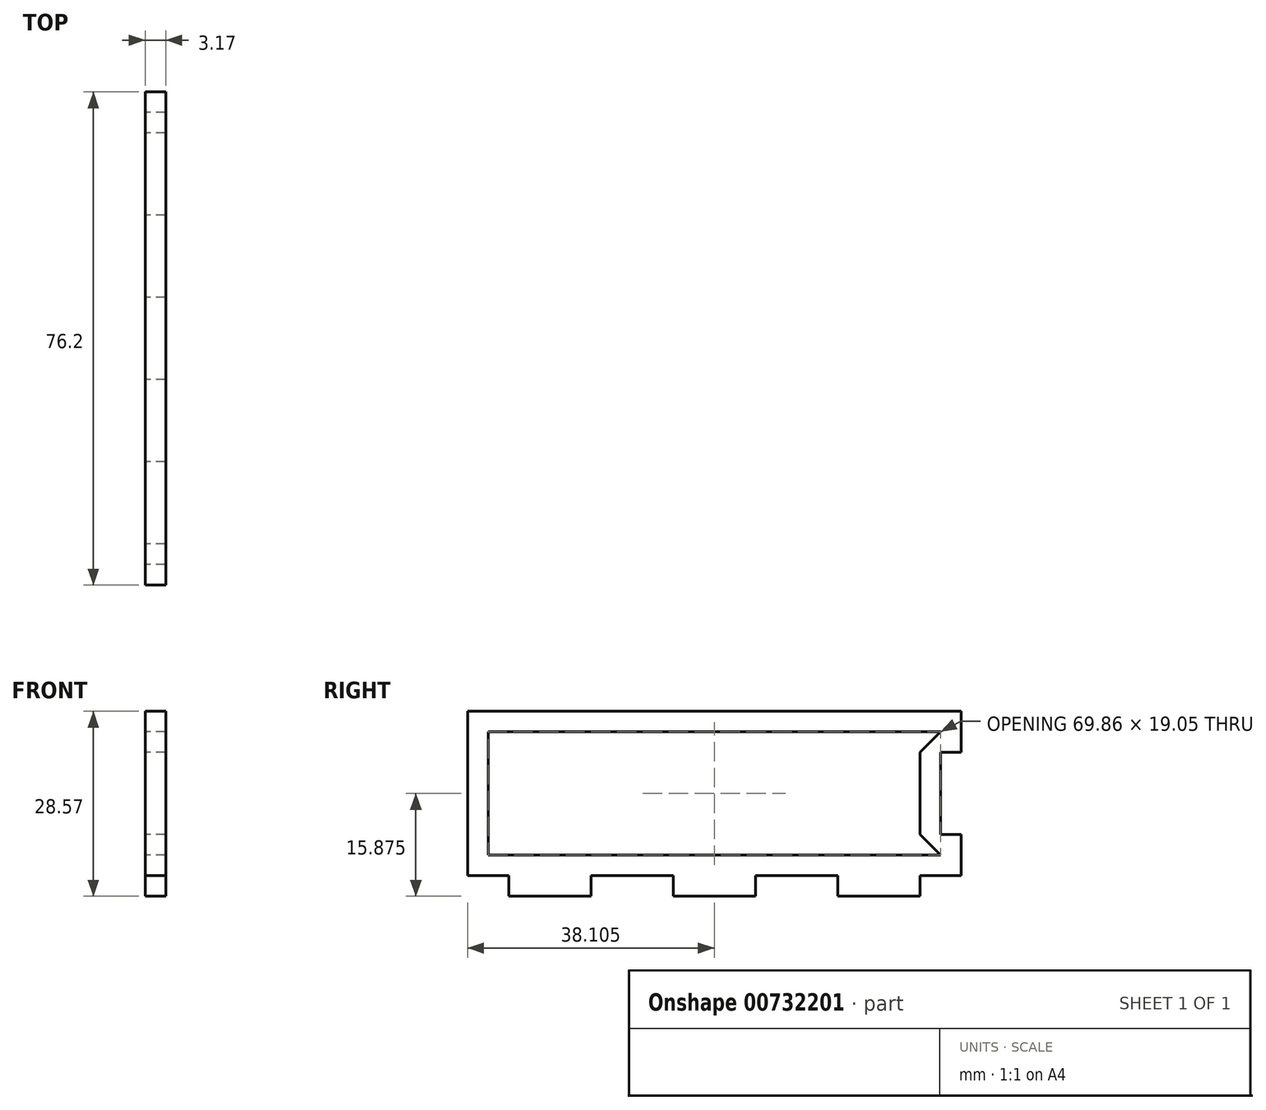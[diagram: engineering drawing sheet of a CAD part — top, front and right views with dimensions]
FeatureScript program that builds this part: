
annotation { "Feature Type Name" : "Feature", "Feature Type Description" : "" }
export const myFeature = defineFeature(function(context is Context, id is Id, definition is map)
    precondition{}
    {
        {
            var Q0;
            Q0=qCreatedBy(makeId("Right.planeOp"),FACE);
            var sketch = newSketch(context, id + "F0", { "sketchPlane" : qUnion([Q0])});
            skLineSegment(sketch, "E0", {"start": v(0, 0) * mm, "end": v(-63.5, 0) * mm});
            skLineSegment(sketch, "E1", {"start": v(-63.5, 0) * mm, "end": v(-63.5, 3.17) * mm});
            skLineSegment(sketch, "E2", {"start": v(-63.5, 3.17) * mm, "end": v(-69.85, 3.17) * mm});
            skLineSegment(sketch, "E3", {"start": v(0, 0) * mm, "end": v(0, 3.18) * mm});
            skLineSegment(sketch, "E4", {"start": v(0, 3.18) * mm, "end": v(6.35, 3.18) * mm});
            skLineSegment(sketch, "E5", {"start": v(6.35, 3.18) * mm, "end": v(6.35, 28.58) * mm});
            skLineSegment(sketch, "E6", {"start": v(6.35, 28.58) * mm, "end": v(-69.85, 28.58) * mm});
            skLineSegment(sketch, "E7", {"start": v(-69.85, 28.58) * mm, "end": v(-69.85, 3.17) * mm});
            skLineSegment(sketch, "E8", {"start": v(-63.5, 0) * mm, "end": v(-50.8, 0) * mm});
            skLineSegment(sketch, "E9", {"start": v(-50.8, 0) * mm, "end": v(-50.8, 3.17) * mm});
            skLineSegment(sketch, "E10", {"start": v(-50.8, 3.17) * mm, "end": v(-38.1, 3.17) * mm});
            skLineSegment(sketch, "E11", {"start": v(-38.1, 3.17) * mm, "end": v(-38.1, 0) * mm});
            skLineSegment(sketch, "E12", {"start": v(-38.1, 0) * mm, "end": v(-25.4, 0) * mm});
            skLineSegment(sketch, "E13", {"start": v(-25.4, 0) * mm, "end": v(-25.4, 3.17) * mm});
            skLineSegment(sketch, "E14", {"start": v(-25.4, 3.17) * mm, "end": v(-12.7, 3.17) * mm});
            skLineSegment(sketch, "E15", {"start": v(-12.7, 3.17) * mm, "end": v(-12.7, 0) * mm});
            skLineSegment(sketch, "E16", {"start": v(6.35, 28.58) * mm, "end": v(6.35, 22.23) * mm});
            skLineSegment(sketch, "E17", {"start": v(6.35, 22.23) * mm, "end": v(3.18, 22.23) * mm});
            skLineSegment(sketch, "E18", {"start": v(3.18, 22.23) * mm, "end": v(3.18, 9.53) * mm});
            skLineSegment(sketch, "E19", {"start": v(3.18, 9.53) * mm, "end": v(6.35, 9.53) * mm});
            skLineSegment(sketch, "E20", {"start": v(-69.85, 28.58) * mm, "end": v(-69.85, 25.4) * mm});
            skLineSegment(sketch, "E21", {"start": v(-69.85, 25.4) * mm, "end": v(-66.67, 25.4) * mm});
            skLineSegment(sketch, "E22", {"start": v(-66.67, 25.4) * mm, "end": v(-66.67, 6.35) * mm});
            skLineSegment(sketch, "E23", {"start": v(-66.67, 6.35) * mm, "end": v(3.18, 6.35) * mm});
            skLineSegment(sketch, "E24", {"start": v(3.18, 6.35) * mm, "end": v(0, 9.53) * mm});
            skLineSegment(sketch, "E25", {"start": v(0, 9.53) * mm, "end": v(0, 22.23) * mm});
            skLineSegment(sketch, "E26", {"start": v(0, 22.23) * mm, "end": v(3.18, 25.4) * mm});
            skLineSegment(sketch, "E27", {"start": v(3.18, 25.4) * mm, "end": v(-66.67, 25.4) * mm});
            skSolve(sketch);
        }
        {
            var Q0;
            {var subQ11=sQuery(id+"F0.wireOp",EDGE,"E1");Q0=makeQuery(id+"F0.imprint","IMPRINT",FACE,{"disambiguationData":[TD([[makeQuery(id+"F0.imprint","IMPRINT",EDGE,{"derivedFrom":subQ11}),-1.0]])]});}
            extrude(context, id + "F1", {"entities" : qUnion([Q0]), "depth" : 3.17 * mm, "offsetDistance" : 25.4 * mm});
        }
    });
